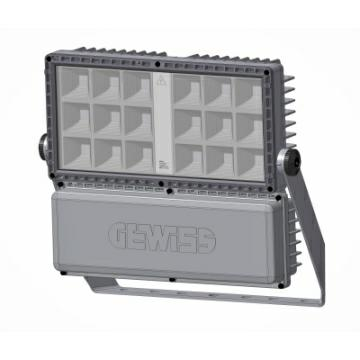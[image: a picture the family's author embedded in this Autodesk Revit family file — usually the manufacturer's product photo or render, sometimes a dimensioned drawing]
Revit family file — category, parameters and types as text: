
# Revit family: Lighting-Proiezione-GEWISS-SMART[PRO]2.0-PROIETTORI-LED-MEDIA-POTENZA_1MODULI_CLI
name_source: partatom
category: Apparecchi per illuminazione
units: mm (PartAtom-declared; Revit-internal decimal feet)

## family parameters
Condiviso = No
Host = Superficie
Punto di calcolo locali = Sì
Quota connettore circolare = Usa diametro
Sorgente d'illuminazione = No
Taglio con vuoti quando caricato = No
Tipo di parte = Normale

## types (1)
- Lighting-Proiezione-GEWISS-SMART[PRO]2.0-PROIETTORI-LED-MEDIA-POTENZA_1MODULI_CLI
    Alimentatore = Incluso
    Apparecchio a ridotta temperatura superficiale = Si
    Applicazione = Interno / Esterno
    Cablaggio = Connettore stagno
    Caratteristiche elettriche e gestione della luce = -
    Caratteristiche ottiche e illuminotecniche = -
    Catalogo = LIGHTING
    Catalogo Serie = SMART [PRO] 2.0
    Certificazione DIN 18032-3 = Si
    Certificazioni e classificazioni = -
    Classe fotobiologica = -
    Classe isolamento = I
    Classificazione: = -
    Codice digitale univoco (Datamatrix) = Attualmente non presente
    Colore = Grigio grafite
    Contesto = Illuminazione di grandi aree, impianti sportivi
    Controllo abbagliamento e luminanza = G*6 - ULOR = 0
    Corpo = Alluminio pressofuso
    Corrente di pilotaggio LED = 0,7 A
    Descrizione = SMART PRO 1M 5700K CRI70 TYPE C1 1-10V
    Dispositivo di protezione = DM 6 kV / CM 10 kV
    Distanza minima dall'oggetto illuminato = 1M
    Durata di vita = L90B10 (Tq+25°C) - 50000h L90B10 (Tq+40°C) = 40000h L80B10 (Tq+25°C) - 110000h
    Efficienza luminosa (lm/W) = 121
    Finitura colore = Verniciato a polvere poliestere
    Fissaggio = Staffa
    Flusso nominale = 24000
    Frequenza nominale (Hz) = 50 / 60
    GW - Codice Electrocod = 2424
    Gancio di chiusura = Viti metriche esagonali
    Garanzia = 5 anni
    Grado di protezione = IP66
    Gruppo ottico = Riflettore in PC HT quarzato&nbsp; e metallizzato lucido
    Guarnizioni = silicone antinvecchiamento
    IDF = 2e96a973-5bee-4609-8733-357f06392928
    IDT = 81921acd85944d64b14f91977cfd80f8
    IPEA = STRADALE = A++ // GRANDI AREE = A5+ // CICLOPEDONALI = A++ // AREE VERDI = A++ // CENTRO STORICO = A7+ // ALTRO = A7+
    Immagine tipo = SMARTPRO20_1M.jpg
    Inclinazione = Rotazione su staffa con goniometro integrato
    Indice di resa cromatica = CRI-70
    Informazioni generali = -
    Installazione e manutenzione = -
    Lampada: = LED
    Life Time L80B10 (Tq 25°C) = >110000 H
    Life Time L90B10 (Tq 25°C) : = >50000 H
    Life Time L90B10 (Tq 40°C) = 40000 H
    Lumen output (lm) = 20000
    Materiali = -
    Modello = GWP2175MS
    Norma di riferimento = EN60598-1; EN60598-2-5; EN60598-2-24; IEC 62778; IEC62471; EN13201
    Numero moduli = 1
    Ottica = C1 - Circolare 30°
    Peso (kg): = 5,7
    Potenza di sistema = 165W
    Produttore = GEWISS S.p.A.
    Prospetto di default = 1219 mm
    Regolazione inclinazione = -120° ÷ + 120° staffa
    Resistenza agli urti = IK08
    Resistenza al filo incandescente = -
    Resistenza alle sovratensioni : = 10KV in modalità comune; 6KV in modalità differenziale
    SEO = Proiettore
    Scheda Tecnica = https://www.gewiss.com
    Schermo = Vetro piano extrachiaro spessore 4mm
    Sistema di controllo = Stand Alone - 1/10V
    Sostituibilità gruppo ottico = Non disponibile
    Sostituibilità piastra di cablaggio = Non disponibile
    Superficie massima esposta al vento = 0,085M2
    Superficie massima esposta al vento : = 0,085 m2
    Temperatura di colore = 5700K
    Temperatura di colore: = 5700 K (CRI>70)
    Temperatura di esercizio = -30 +40 °C
    Temperatura di stoccaggio = -
    Temperatura di utilizzo = -30 +40 °C
    Tensione = 220 / 240 V - 50 / 60 Hz
    Tensione di alimentazione = 220 - 240 V
    Tipo di apparecchio = Apparecchio per proiezione LED di piccola, media e alta potenza
    Tipo di installazione e montaggio = Torrefaro - Parete - Terra
    Tipologia = Stand Alone - 1/10V
    Tipologia sorgente luminosa = LED - Non sostituibile
    Tolleranza cromatica = SDCM = 5
    URL = https://www.gewiss.com
    Vano di alimentazione = Integrato
    Versione file RFA = 20.11
    Versioni = Luce fredda 5700K
    Viti esterne = Acciaio inossidabile
